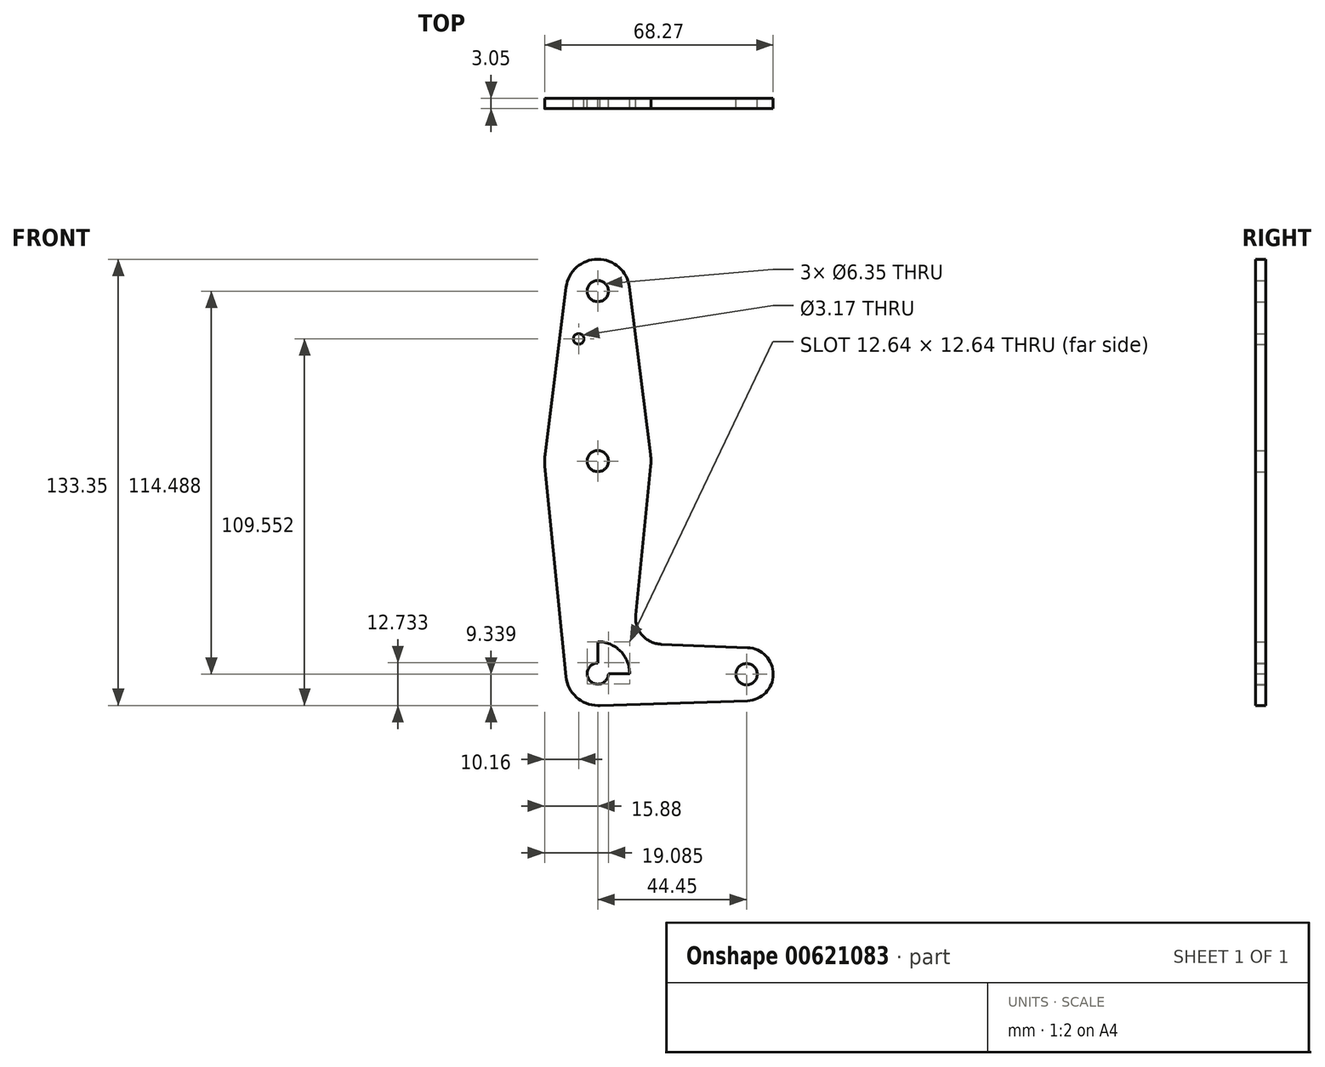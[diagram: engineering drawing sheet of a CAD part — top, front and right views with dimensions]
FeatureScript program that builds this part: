
annotation { "Feature Type Name" : "Feature", "Feature Type Description" : "" }
export const myFeature = defineFeature(function(context is Context, id is Id, definition is map)
    precondition{}
    {
        {
            var Q0;
            Q0=qCreatedBy(makeId("Front.planeOp"),FACE);
            var sketch = newSketch(context, id + "F0", { "sketchPlane" : qUnion([Q0])});
            skLineSegment(sketch, "E0", {"start": v(0, 71.65) * mm, "end": v(0, -42.65) * mm});
            skCircle(sketch, "E1", {"center": v(0, 71.65) * mm, "radius": 9.53 * mm});
            skCircle(sketch, "E2", {"center": v(0, 20.85) * mm, "radius": 15.88 * mm});
            skCircle(sketch, "E3", {"center": v(0, -42.65) * mm, "radius": 9.53 * mm});
            skCircle(sketch, "E4", {"center": v(44.45, -42.84) * mm, "radius": 7.94 * mm});
            skLineSegment(sketch, "E5", {"start": v(0, 20.85) * mm, "end": v(0, -42.65) * mm});
            skLineSegment(sketch, "E6", {"start": v(15.75, 22.83) * mm, "end": v(9.45, 72.84) * mm});
            skLineSegment(sketch, "E7", {"start": v(-9.45, 72.84) * mm, "end": v(-15.75, 22.83) * mm});
            skLineSegment(sketch, "E8", {"start": v(18.93, -33.88) * mm, "end": v(44.77, -34.9) * mm});
            skLineSegment(sketch, "E9", {"start": v(0, -52.18) * mm, "end": v(44.77, -50.77) * mm});
            skLineSegment(sketch, "E10", {"start": v(-15.8, 19.26) * mm, "end": v(-9.48, -43.6) * mm});
            skLineSegment(sketch, "E11", {"start": v(15.8, 19.26) * mm, "end": v(11.33, -25.14) * mm});
            skLineSegment(sketch, "E12", {"start": v(0, -42.65) * mm, "end": v(44.45, -42.84) * mm});
            skCircle(sketch, "E13", {"center": v(0, 71.65) * mm, "radius": 3.18 * mm});
            skCircle(sketch, "E14", {"center": v(0, 20.85) * mm, "radius": 3.18 * mm});
            skCircle(sketch, "E15", {"center": v(0, -42.65) * mm, "radius": 3.18 * mm});
            skCircle(sketch, "E16", {"center": v(44.45, -42.84) * mm, "radius": 3.18 * mm});
            skCircle(sketch, "E17", {"center": v(-5.72, 57.37) * mm, "radius": 1.59 * mm});
            skPoint(sketch, "E18.newPointB", {"position": v(0, -33.13) * mm});
            skArc(sketch, "E18.filletArc", {"start": v(11.33, -25.14) * mm, "mid": v(13.24, -31.15) * mm, "end": v(18.93, -33.88) * mm});
            skSolve(sketch);
        }
        {
            var Q0;
            Q0 = qSketchRegion(id + "F0", true);
            extrude(context, id + "F1", {"entities" : qUnion([Q0]), "depth" : 3.05 * mm, "offsetDistance" : 25.4 * mm});
        }
        {
            var Q0;
            {var subQ0=sQuery(id+"F0.wireOp",EDGE,"E5");var subQ1=sQuery(id+"F0.wireOp",EDGE,"E3");var subQ2=makeQuery(id+"F0.imprint","INTERSECT",VERTEX,{"derivedFrom":[subQ1,subQ0]});Q0=makeQuery(id+"F0.imprint","IMPRINT",FACE,{"disambiguationData":[TD([[makeQuery(id+"F0.imprint","IMPRINT",EDGE,{"disambiguationData":[TD([[subQ2,1.0]])],"derivedFrom":subQ1}),1.0]])]});}
            extrude(context, id + "F2", {"entities" : qUnion([Q0]), "operationType" : NewBodyOperationType.ADD, "depth" : 3.05 * mm, "offsetDistance" : 25.4 * mm});
        }
    });
